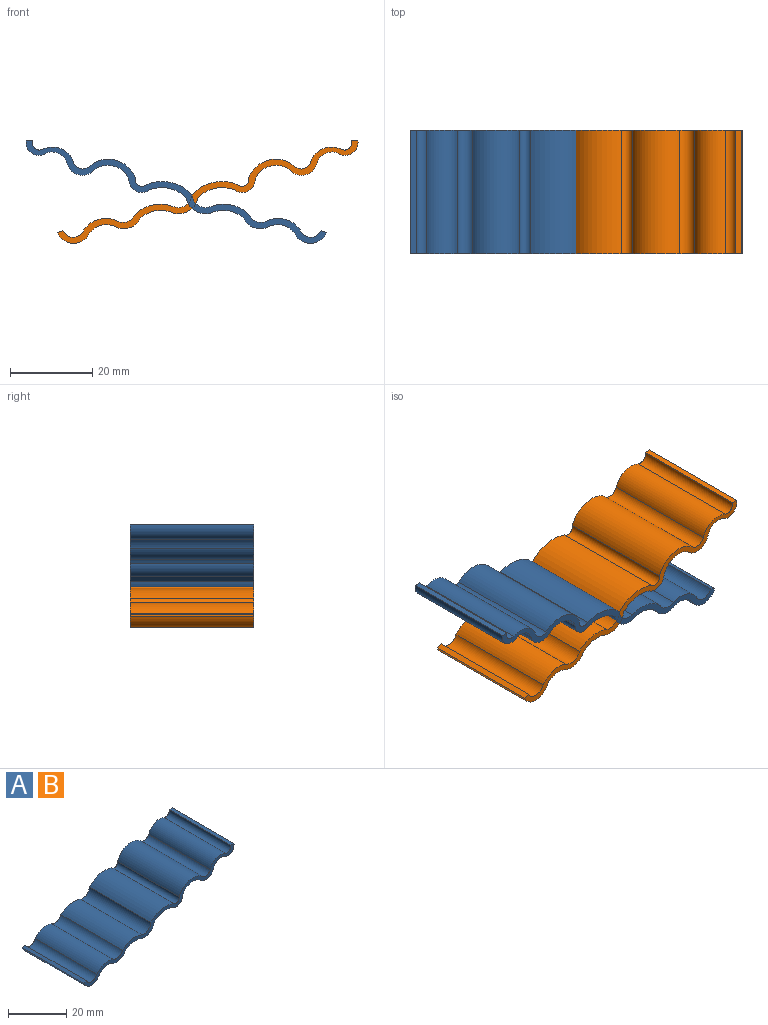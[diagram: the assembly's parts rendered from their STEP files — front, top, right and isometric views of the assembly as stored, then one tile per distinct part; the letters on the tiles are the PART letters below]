
ASSEMBLY  parts=2 mates=1
PART A: 26 faces, bbox 73.2x30x25.1 mm
  f0: cylinder r=2.39mm len=30mm, axis (0,1,0), area 128.6mm2, adj f1,f23,f24,f25
  f1: cylinder r=7.03mm len=30mm, axis (0,1,0), area 424.1mm2, adj f0,f2,f24,f25
  f2: cylinder r=1.6mm len=30mm, axis (0,1,0), area 123.2mm2, adj f1,f3,f24,f25
  f3: cylinder r=10.03mm len=30mm, axis (0,1,0), area 360mm2, adj f2,f4,f24,f25
  f4: cylinder r=3.35mm len=30mm, axis (0,1,0), area 183.7mm2, adj f3,f5,f24,f25
  f5: cylinder r=8.71mm len=30mm, axis (0,1,0), area 306mm2, adj f4,f6,f24,f25
  f6: cylinder r=3.18mm len=30mm, axis (0,1,0), area 167.5mm2, adj f5,f7,f24,f25
  f7: cylinder r=6.62mm len=30mm, axis (0,1,0), area 265mm2, adj f6,f8,f24,f25
  f8: cylinder r=2.76mm len=30mm, axis (0,1,0), area 197mm2, adj f7,f9,f24,f25
  f9: plane 30x1.32mm, normal (-0.39,0,0.92), area 43mm2, adj f8,f10,f24,f25
  f10: cylinder r=4.26mm len=30mm, axis (0,1,0), area 298.3mm2, adj f9,f11,f24,f25
  f11: cylinder r=5.12mm len=30mm, axis (0,1,0), area 196.4mm2, adj f10,f12,f24,f25
  f12: cylinder r=4.68mm len=30mm, axis (0,1,0), area 230.9mm2, adj f11,f13,f24,f25
  f13: cylinder r=7.21mm len=30mm, axis (0,1,0), area 247mm2, adj f12,f14,f24,f25
  f14: cylinder r=4.85mm len=30mm, axis (0,1,0), area 249.8mm2, adj f13,f15,f24,f25
  f15: cylinder r=8.53mm len=30mm, axis (0,1,0), area 284.3mm2, adj f14,f16,f24,f25
  f16: cylinder r=3.1mm len=30mm, axis (0,1,0), area 212.4mm2, adj f15,f17,f24,f25
  f17: cylinder r=5.53mm len=30mm, axis (0,1,0), area 327.6mm2, adj f16,f18,f24,f25
  f18: cylinder r=3.89mm len=30mm, axis (0,1,0), area 216.6mm2, adj f17,f19,f24,f25
  f19: cylinder r=3.77mm len=30mm, axis (0,1,0), area 203.6mm2, adj f18,f20,f24,f25
  f20: cylinder r=3.11mm len=30mm, axis (0,1,0), area 217mm2, adj f19,f21,f24,f25
  f21: plane 30x1.5mm, normal (0,0,1), area 45mm2, adj f20,f22,f24,f25
  f22: cylinder r=1.87mm len=30mm, axis (0,1,0), area 122.7mm2, adj f21,f23,f24,f25
  f23: cylinder r=5.27mm len=30mm, axis (0,1,0), area 280.5mm2, adj f0,f22,f24,f25
  f24: plane 73.18x25.06mm, normal (0,-1,0), area 130.3mm2, adj f0,f1,f2,f3,f4,f5,f6,f7
  f25: plane 73.18x25.06mm, normal (0,1,0), area 130.3mm2, adj f0,f1,f2,f3,f4,f5,f6,f7
PART B: same geometry as A
PLACE A rot(axis=(0,0,1),180deg) t=(258.77,-574.98,61.7)mm
PLACE B t=(-184.53,595.02,61.7)mm fixed
MATE fastened A.f24 <-> B.f25  axis (0,1,0) through (37.12,25.02,8.78)mm
